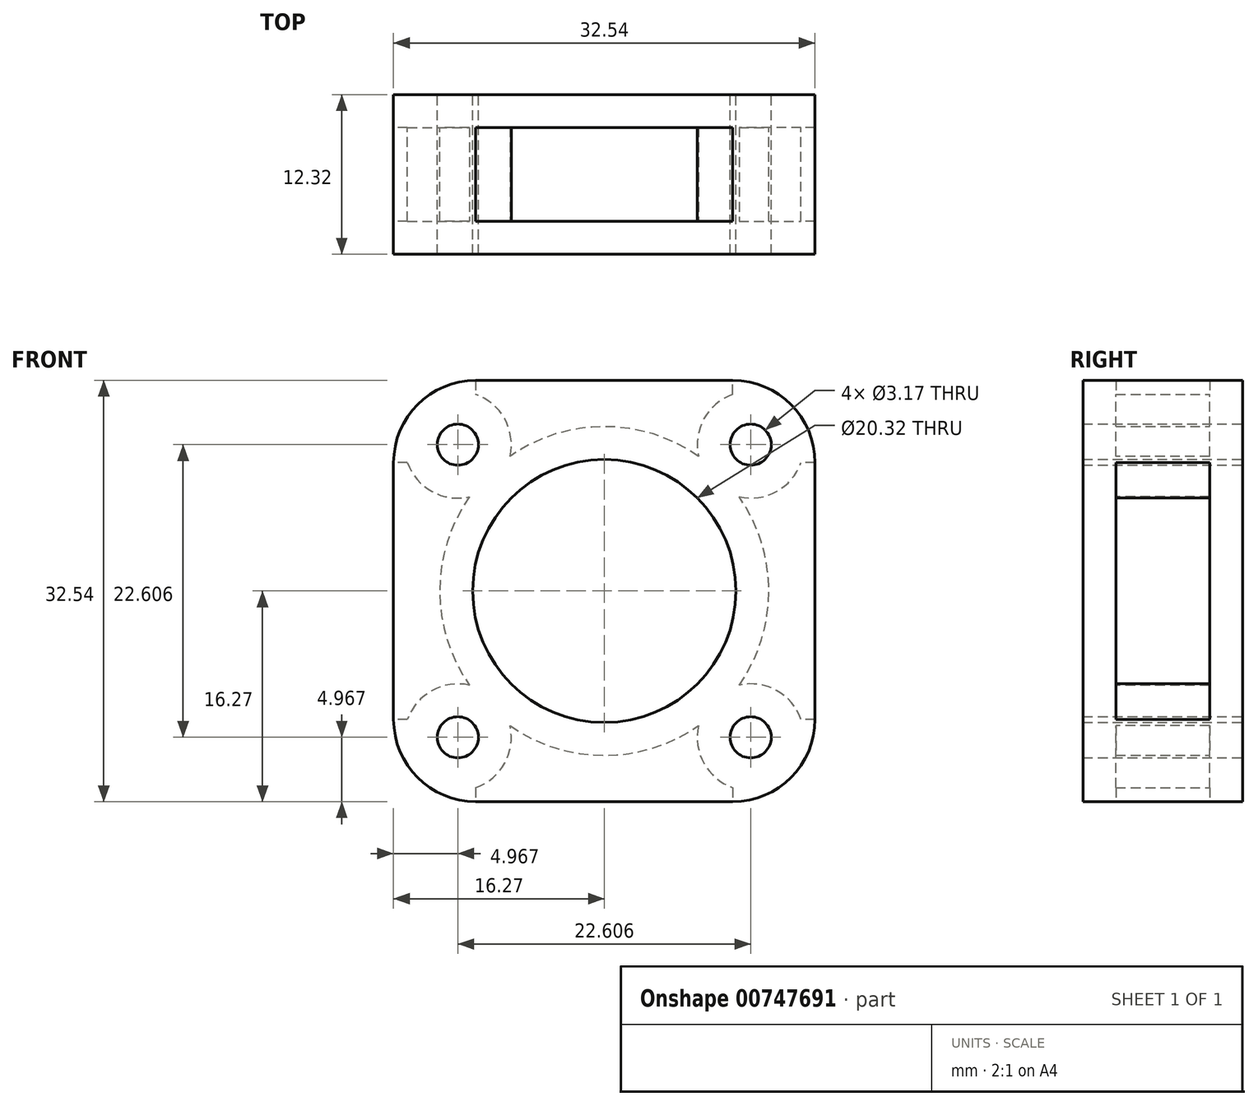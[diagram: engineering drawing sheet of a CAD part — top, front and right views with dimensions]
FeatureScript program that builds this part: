
annotation { "Feature Type Name" : "Feature", "Feature Type Description" : "" }
export const myFeature = defineFeature(function(context is Context, id is Id, definition is map)
    precondition{}
    {
        {
            var Q0;
            Q0=qCreatedBy(makeId("Front.planeOp"),FACE);
            var sketch = newSketch(context, id + "F0", { "sketchPlane" : qUnion([Q0]), "disableImprinting" : false});
            skLineSegment(sketch, "E0.bottom", {"start": v(-9.92, 16.27) * mm, "end": v(9.92, 16.27) * mm});
            skLineSegment(sketch, "E0.top", {"start": v(-9.92, -16.27) * mm, "end": v(9.92, -16.27) * mm});
            skLineSegment(sketch, "E0.left", {"start": v(-16.27, 9.92) * mm, "end": v(-16.27, -9.92) * mm});
            skLineSegment(sketch, "E0.right", {"start": v(16.27, 9.92) * mm, "end": v(16.27, -9.92) * mm});
            skPoint(sketch, "E0.middle", {"position": v(0, 0) * mm});
            skCircle(sketch, "E1", {"center": v(0, 0) * mm, "radius": 10.16 * mm});
            skCircle(sketch, "E2", {"center": v(-11.3, 11.3) * mm, "radius": 1.59 * mm});
            skCircle(sketch, "E3", {"center": v(11.3, 11.3) * mm, "radius": 1.59 * mm});
            skCircle(sketch, "E4", {"center": v(-11.3, -11.3) * mm, "radius": 1.59 * mm});
            skCircle(sketch, "E5", {"center": v(11.3, -11.3) * mm, "radius": 1.59 * mm});
            skPoint(sketch, "E6.visualSharp", {"position": v(-16.27, 16.27) * mm});
            skArc(sketch, "E6.filletArc", {"start": v(-9.92, 16.27) * mm, "mid": v(-14.4, 14.4) * mm, "end": v(-16.27, 9.92) * mm});
            skPoint(sketch, "E7.visualSharp", {"position": v(16.27, 16.27) * mm});
            skArc(sketch, "E7.filletArc", {"start": v(16.27, 9.92) * mm, "mid": v(14.4, 14.4) * mm, "end": v(9.92, 16.27) * mm});
            skPoint(sketch, "E8.visualSharp", {"position": v(16.27, -16.27) * mm});
            skArc(sketch, "E8.filletArc", {"start": v(9.92, -16.27) * mm, "mid": v(14.4, -14.4) * mm, "end": v(16.27, -9.92) * mm});
            skPoint(sketch, "E9.visualSharp", {"position": v(-16.27, -16.27) * mm});
            skArc(sketch, "E9.filletArc", {"start": v(-16.27, -9.92) * mm, "mid": v(-14.4, -14.4) * mm, "end": v(-9.92, -16.27) * mm});
            skSolve(sketch);
        }
        {
            var Q0;
            Q0=makeQuery(id+"F0.imprint","IMPRINT",FACE,{"disambiguationData":[TD([[makeQuery(id+"F0.imprint","IMPRINT",EDGE,{"derivedFrom":sQuery(id+"F0.wireOp",EDGE,"E0.bottom")}),-1.0]])]});
            extrude(context, id + "F1", {"entities" : qUnion([Q0]), "depth" : 12.32 * mm, "offsetDistance" : 25.4 * mm});
        }
        {
            var Q0;
            Q0=makeQuery(id+"F1.opExtrude","SWEPT_FACE",FACE,{"disambiguationData":[OSD([sQuery(id+"F0.wireOp",EDGE,"E0.top")])]});
            var Q1;
            Q1=makeQuery(id+"F1.opExtrude","SWEPT_FACE",FACE,{"disambiguationData":[OSD([sQuery(id+"F0.wireOp",EDGE,"E0.right")])]});
            var Q2;
            Q2=makeQuery(id+"F1.opExtrude","SWEPT_FACE",FACE,{"disambiguationData":[OSD([sQuery(id+"F0.wireOp",EDGE,"E0.bottom")])]});
            var Q3;
            Q3=makeQuery(id+"F1.opExtrude","SWEPT_FACE",FACE,{"disambiguationData":[OSD([sQuery(id+"F0.wireOp",EDGE,"E0.left")])]});
            shell(context, id + "F2", {"entities" : qUnion([Q0, Q1, Q2, Q3]), "thickness" : 2.54 * mm});
        }
    });
